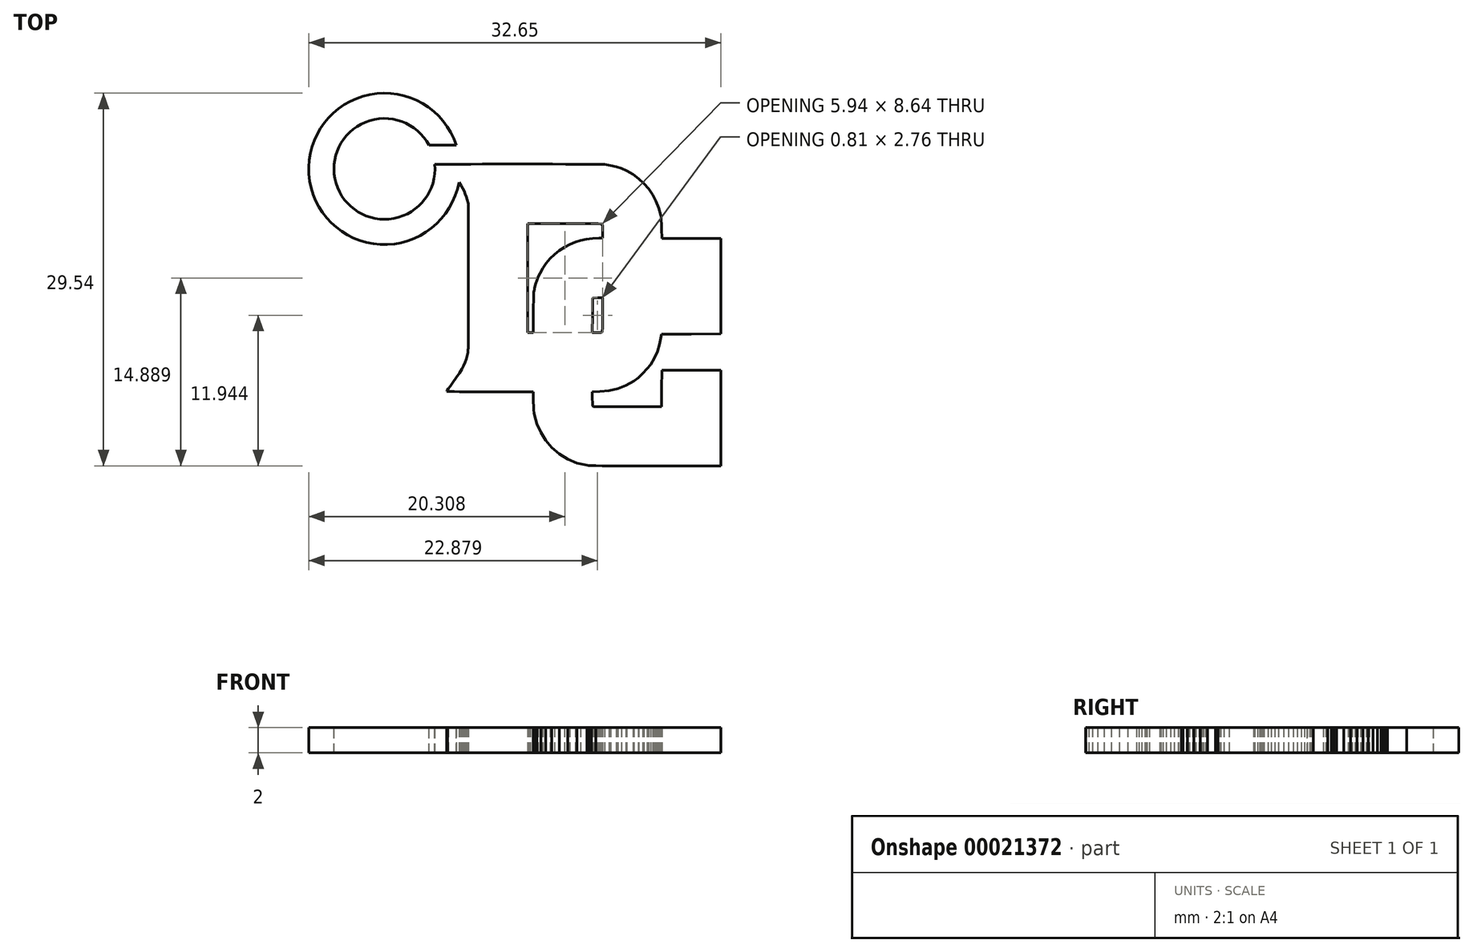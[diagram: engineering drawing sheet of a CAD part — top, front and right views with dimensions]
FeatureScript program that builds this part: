
annotation { "Feature Type Name" : "Feature", "Feature Type Description" : "" }
export const myFeature = defineFeature(function(context is Context, id is Id, definition is map)
    precondition{}
    {
        {
            var Q0;
            Q0=qCreatedBy(makeId("Top.planeOp"),FACE);
            var sketch = newSketch(context, id + "F0", { "sketchPlane" : qUnion([Q0])});
            skLineSegment(sketch, "E0", {"start": v(0.24, -11.91) * mm, "end": v(-0.53, -11.73) * mm});
            skLineSegment(sketch, "E1", {"start": v(-0.53, -11.73) * mm, "end": v(-1.26, -11.43) * mm});
            skLineSegment(sketch, "E2", {"start": v(-1.26, -11.43) * mm, "end": v(-1.93, -11.02) * mm});
            skLineSegment(sketch, "E3", {"start": v(-1.93, -11.02) * mm, "end": v(-2.53, -10.5) * mm});
            skLineSegment(sketch, "E4", {"start": v(-2.53, -10.5) * mm, "end": v(-3.02, -9.94) * mm});
            skLineSegment(sketch, "E5", {"start": v(-3.02, -9.94) * mm, "end": v(-3.41, -9.31) * mm});
            skLineSegment(sketch, "E6", {"start": v(-3.41, -9.31) * mm, "end": v(-3.72, -8.64) * mm});
            skLineSegment(sketch, "E7", {"start": v(-3.72, -8.64) * mm, "end": v(-3.92, -7.93) * mm});
            skLineSegment(sketch, "E8", {"start": v(-3.92, -7.93) * mm, "end": v(-3.95, -7.76) * mm});
            skLineSegment(sketch, "E9", {"start": v(-3.95, -7.76) * mm, "end": v(-3.97, -7.53) * mm});
            skLineSegment(sketch, "E10", {"start": v(-3.97, -7.53) * mm, "end": v(-3.98, -7.24) * mm});
            skLineSegment(sketch, "E11", {"start": v(-3.98, -7.24) * mm, "end": v(-4, -6.88) * mm});
            skLineSegment(sketch, "E12", {"start": v(-4, -6.88) * mm, "end": v(-4.01, -6.1) * mm});
            skLineSegment(sketch, "E13", {"start": v(-4.01, -6.1) * mm, "end": v(-7.44, -6.09) * mm});
            skLineSegment(sketch, "E14", {"start": v(-7.44, -6.09) * mm, "end": v(-8.12, -6.09) * mm});
            skLineSegment(sketch, "E15", {"start": v(-8.12, -6.09) * mm, "end": v(-8.77, -6.08) * mm});
            skLineSegment(sketch, "E16", {"start": v(-8.77, -6.08) * mm, "end": v(-9.35, -6.08) * mm});
            skLineSegment(sketch, "E17", {"start": v(-9.35, -6.08) * mm, "end": v(-9.85, -6.08) * mm});
            skLineSegment(sketch, "E18", {"start": v(-9.85, -6.08) * mm, "end": v(-10.27, -6.07) * mm});
            skLineSegment(sketch, "E19", {"start": v(-10.27, -6.07) * mm, "end": v(-10.59, -6.07) * mm});
            skLineSegment(sketch, "E20", {"start": v(-10.59, -6.07) * mm, "end": v(-10.79, -6.07) * mm});
            skLineSegment(sketch, "E21", {"start": v(-10.79, -6.07) * mm, "end": v(-10.86, -6.06) * mm});
            skLineSegment(sketch, "E22", {"start": v(-10.86, -6.06) * mm, "end": v(-10.82, -6) * mm});
            skLineSegment(sketch, "E23", {"start": v(-10.82, -6) * mm, "end": v(-10.72, -5.85) * mm});
            skLineSegment(sketch, "E24", {"start": v(-10.72, -5.85) * mm, "end": v(-10.57, -5.63) * mm});
            skLineSegment(sketch, "E25", {"start": v(-10.57, -5.63) * mm, "end": v(-10.38, -5.37) * mm});
            skLineSegment(sketch, "E26", {"start": v(-10.38, -5.37) * mm, "end": v(-10.09, -4.96) * mm});
            skLineSegment(sketch, "E27", {"start": v(-10.09, -4.96) * mm, "end": v(-9.85, -4.6) * mm});
            skLineSegment(sketch, "E28", {"start": v(-9.85, -4.6) * mm, "end": v(-9.66, -4.3) * mm});
            skLineSegment(sketch, "E29", {"start": v(-9.66, -4.3) * mm, "end": v(-9.51, -4.01) * mm});
            skLineSegment(sketch, "E30", {"start": v(-9.51, -4.01) * mm, "end": v(-9.4, -3.75) * mm});
            skLineSegment(sketch, "E31", {"start": v(-9.4, -3.75) * mm, "end": v(-9.3, -3.5) * mm});
            skLineSegment(sketch, "E32", {"start": v(-9.3, -3.5) * mm, "end": v(-9.24, -3.24) * mm});
            skLineSegment(sketch, "E33", {"start": v(-9.24, -3.24) * mm, "end": v(-9.18, -2.97) * mm});
            skLineSegment(sketch, "E34", {"start": v(-9.18, -2.97) * mm, "end": v(-9.18, -2.9) * mm});
            skLineSegment(sketch, "E35", {"start": v(-9.18, -2.9) * mm, "end": v(-9.17, -2.84) * mm});
            skLineSegment(sketch, "E36", {"start": v(-9.17, -2.84) * mm, "end": v(-9.16, -2.75) * mm});
            skLineSegment(sketch, "E37", {"start": v(-9.16, -2.75) * mm, "end": v(-9.16, -2.63) * mm});
            skLineSegment(sketch, "E38", {"start": v(-9.16, -2.63) * mm, "end": v(-9.15, -2.48) * mm});
            skLineSegment(sketch, "E39", {"start": v(-9.15, -2.48) * mm, "end": v(-9.15, -2.29) * mm});
            skLineSegment(sketch, "E40", {"start": v(-9.15, -2.29) * mm, "end": v(-9.15, -2.05) * mm});
            skLineSegment(sketch, "E41", {"start": v(-9.15, -2.05) * mm, "end": v(-9.14, -1.77) * mm});
            skLineSegment(sketch, "E42", {"start": v(-9.14, -1.77) * mm, "end": v(-9.14, -1.42) * mm});
            skLineSegment(sketch, "E43", {"start": v(-9.14, -1.42) * mm, "end": v(-9.14, -1.02) * mm});
            skLineSegment(sketch, "E44", {"start": v(-9.14, -1.02) * mm, "end": v(-9.14, -0.54) * mm});
            skLineSegment(sketch, "E45", {"start": v(-9.14, -0.54) * mm, "end": v(-9.14, 0) * mm});
            skLineSegment(sketch, "E46", {"start": v(-9.14, 0) * mm, "end": v(-9.14, 0.64) * mm});
            skLineSegment(sketch, "E47", {"start": v(-9.14, 0.64) * mm, "end": v(-9.14, 1.36) * mm});
            skLineSegment(sketch, "E48", {"start": v(-9.14, 1.36) * mm, "end": v(-9.14, 2.17) * mm});
            skLineSegment(sketch, "E49", {"start": v(-9.14, 2.17) * mm, "end": v(-9.14, 3.09) * mm});
            skLineSegment(sketch, "E50", {"start": v(-9.14, 3.09) * mm, "end": v(-9.15, 8.83) * mm});
            skLineSegment(sketch, "E51", {"start": v(-9.15, 8.83) * mm, "end": v(-9.24, 9.14) * mm});
            skLineSegment(sketch, "E52", {"start": v(-9.24, 9.14) * mm, "end": v(-9.3, 9.38) * mm});
            skLineSegment(sketch, "E53", {"start": v(-9.3, 9.38) * mm, "end": v(-9.39, 9.6) * mm});
            skLineSegment(sketch, "E54", {"start": v(-9.39, 9.6) * mm, "end": v(-9.48, 9.81) * mm});
            skLineSegment(sketch, "E55", {"start": v(-9.48, 9.81) * mm, "end": v(-9.59, 10.03) * mm});
            skLineSegment(sketch, "E56", {"start": v(-9.59, 10.03) * mm, "end": v(-9.72, 10.26) * mm});
            skLineSegment(sketch, "E57", {"start": v(-9.72, 10.26) * mm, "end": v(-9.89, 10.52) * mm});
            skLineSegment(sketch, "E58", {"start": v(-9.89, 10.52) * mm, "end": v(-10.1, 10.83) * mm});
            skLineSegment(sketch, "E59", {"start": v(-10.1, 10.83) * mm, "end": v(-10.34, 11.18) * mm});
            skLineSegment(sketch, "E60", {"start": v(-10.34, 11.18) * mm, "end": v(-10.54, 11.47) * mm});
            skLineSegment(sketch, "E61", {"start": v(-10.54, 11.47) * mm, "end": v(-10.7, 11.7) * mm});
            skLineSegment(sketch, "E62", {"start": v(-10.7, 11.7) * mm, "end": v(-10.82, 11.87) * mm});
            skLineSegment(sketch, "E63", {"start": v(-10.82, 11.87) * mm, "end": v(-10.86, 11.94) * mm});
            skLineSegment(sketch, "E64", {"start": v(-10.86, 11.94) * mm, "end": v(-10.72, 11.94) * mm});
            skLineSegment(sketch, "E65", {"start": v(-10.72, 11.94) * mm, "end": v(-10.34, 11.95) * mm});
            skLineSegment(sketch, "E66", {"start": v(-10.34, 11.95) * mm, "end": v(-9.74, 11.95) * mm});
            skLineSegment(sketch, "E67", {"start": v(-9.74, 11.95) * mm, "end": v(-8.96, 11.96) * mm});
            skLineSegment(sketch, "E68", {"start": v(-8.96, 11.96) * mm, "end": v(-8.03, 11.96) * mm});
            skLineSegment(sketch, "E69", {"start": v(-8.03, 11.96) * mm, "end": v(-7, 11.96) * mm});
            skLineSegment(sketch, "E70", {"start": v(-7, 11.96) * mm, "end": v(-5.9, 11.96) * mm});
            skLineSegment(sketch, "E71", {"start": v(-5.9, 11.96) * mm, "end": v(-4.75, 11.96) * mm});
            skLineSegment(sketch, "E72", {"start": v(-4.75, 11.96) * mm, "end": v(-3.6, 11.96) * mm});
            skLineSegment(sketch, "E73", {"start": v(-3.6, 11.96) * mm, "end": v(-2.47, 11.96) * mm});
            skLineSegment(sketch, "E74", {"start": v(-2.47, 11.96) * mm, "end": v(-1.42, 11.96) * mm});
            skLineSegment(sketch, "E75", {"start": v(-1.42, 11.96) * mm, "end": v(-0.46, 11.95) * mm});
            skLineSegment(sketch, "E76", {"start": v(-0.46, 11.95) * mm, "end": v(0.36, 11.95) * mm});
            skLineSegment(sketch, "E77", {"start": v(0.36, 11.95) * mm, "end": v(1, 11.94) * mm});
            skLineSegment(sketch, "E78", {"start": v(1, 11.94) * mm, "end": v(1.45, 11.94) * mm});
            skLineSegment(sketch, "E79", {"start": v(1.45, 11.94) * mm, "end": v(1.65, 11.93) * mm});
            skLineSegment(sketch, "E80", {"start": v(1.65, 11.93) * mm, "end": v(2.12, 11.86) * mm});
            skLineSegment(sketch, "E81", {"start": v(2.12, 11.86) * mm, "end": v(2.56, 11.76) * mm});
            skLineSegment(sketch, "E82", {"start": v(2.56, 11.76) * mm, "end": v(2.97, 11.61) * mm});
            skLineSegment(sketch, "E83", {"start": v(2.97, 11.61) * mm, "end": v(3.4, 11.42) * mm});
            skLineSegment(sketch, "E84", {"start": v(3.4, 11.42) * mm, "end": v(3.9, 11.14) * mm});
            skLineSegment(sketch, "E85", {"start": v(3.9, 11.14) * mm, "end": v(4.35, 10.8) * mm});
            skLineSegment(sketch, "E86", {"start": v(4.35, 10.8) * mm, "end": v(4.76, 10.42) * mm});
            skLineSegment(sketch, "E87", {"start": v(4.76, 10.42) * mm, "end": v(5.13, 10) * mm});
            skLineSegment(sketch, "E88", {"start": v(5.13, 10) * mm, "end": v(5.45, 9.53) * mm});
            skLineSegment(sketch, "E89", {"start": v(5.45, 9.53) * mm, "end": v(5.71, 9.02) * mm});
            skLineSegment(sketch, "E90", {"start": v(5.71, 9.02) * mm, "end": v(5.93, 8.48) * mm});
            skLineSegment(sketch, "E91", {"start": v(5.93, 8.48) * mm, "end": v(6.08, 7.92) * mm});
            skLineSegment(sketch, "E92", {"start": v(6.08, 7.92) * mm, "end": v(6.12, 7.72) * mm});
            skLineSegment(sketch, "E93", {"start": v(6.12, 7.72) * mm, "end": v(6.14, 7.5) * mm});
            skLineSegment(sketch, "E94", {"start": v(6.14, 7.5) * mm, "end": v(6.16, 7.22) * mm});
            skLineSegment(sketch, "E95", {"start": v(6.16, 7.22) * mm, "end": v(6.17, 6.83) * mm});
            skLineSegment(sketch, "E96", {"start": v(6.17, 6.83) * mm, "end": v(6.19, 6.08) * mm});
            skLineSegment(sketch, "E97", {"start": v(6.19, 6.08) * mm, "end": v(10.86, 6.08) * mm});
            skLineSegment(sketch, "E98", {"start": v(10.86, 6.08) * mm, "end": v(10.86, -1.5) * mm});
            skLineSegment(sketch, "E99", {"start": v(10.86, -1.5) * mm, "end": v(8.51, -1.5) * mm});
            skLineSegment(sketch, "E100", {"start": v(8.51, -1.5) * mm, "end": v(6.16, -1.51) * mm});
            skLineSegment(sketch, "E101", {"start": v(6.16, -1.51) * mm, "end": v(6.14, -1.67) * mm});
            skLineSegment(sketch, "E102", {"start": v(6.14, -1.67) * mm, "end": v(6, -2.31) * mm});
            skLineSegment(sketch, "E103", {"start": v(6, -2.31) * mm, "end": v(5.83, -2.88) * mm});
            skLineSegment(sketch, "E104", {"start": v(5.83, -2.88) * mm, "end": v(5.6, -3.41) * mm});
            skLineSegment(sketch, "E105", {"start": v(5.6, -3.41) * mm, "end": v(5.29, -3.92) * mm});
            skLineSegment(sketch, "E106", {"start": v(5.29, -3.92) * mm, "end": v(5.02, -4.25) * mm});
            skLineSegment(sketch, "E107", {"start": v(5.02, -4.25) * mm, "end": v(4.68, -4.62) * mm});
            skLineSegment(sketch, "E108", {"start": v(4.68, -4.62) * mm, "end": v(4.3, -4.97) * mm});
            skLineSegment(sketch, "E109", {"start": v(4.3, -4.97) * mm, "end": v(3.97, -5.23) * mm});
            skLineSegment(sketch, "E110", {"start": v(3.97, -5.23) * mm, "end": v(3.34, -5.6) * mm});
            skLineSegment(sketch, "E111", {"start": v(3.34, -5.6) * mm, "end": v(2.7, -5.85) * mm});
            skLineSegment(sketch, "E112", {"start": v(2.7, -5.85) * mm, "end": v(2.01, -6) * mm});
            skLineSegment(sketch, "E113", {"start": v(2.01, -6) * mm, "end": v(1.26, -6.07) * mm});
            skLineSegment(sketch, "E114", {"start": v(1.26, -6.07) * mm, "end": v(0.68, -6.09) * mm});
            skLineSegment(sketch, "E115", {"start": v(0.68, -6.09) * mm, "end": v(0.68, -6.65) * mm});
            skLineSegment(sketch, "E116", {"start": v(0.68, -6.65) * mm, "end": v(0.68, -6.92) * mm});
            skLineSegment(sketch, "E117", {"start": v(0.68, -6.92) * mm, "end": v(0.7, -7.1) * mm});
            skLineSegment(sketch, "E118", {"start": v(0.7, -7.1) * mm, "end": v(0.7, -7.2) * mm});
            skLineSegment(sketch, "E119", {"start": v(0.7, -7.2) * mm, "end": v(0.73, -7.25) * mm});
            skLineSegment(sketch, "E120", {"start": v(0.73, -7.25) * mm, "end": v(0.77, -7.26) * mm});
            skLineSegment(sketch, "E121", {"start": v(0.77, -7.26) * mm, "end": v(0.9, -7.26) * mm});
            skLineSegment(sketch, "E122", {"start": v(0.9, -7.26) * mm, "end": v(1.09, -7.27) * mm});
            skLineSegment(sketch, "E123", {"start": v(1.09, -7.27) * mm, "end": v(1.37, -7.27) * mm});
            skLineSegment(sketch, "E124", {"start": v(1.37, -7.27) * mm, "end": v(1.74, -7.28) * mm});
            skLineSegment(sketch, "E125", {"start": v(1.74, -7.28) * mm, "end": v(2.21, -7.28) * mm});
            skLineSegment(sketch, "E126", {"start": v(2.21, -7.28) * mm, "end": v(2.79, -7.28) * mm});
            skLineSegment(sketch, "E127", {"start": v(2.79, -7.28) * mm, "end": v(3.47, -7.27) * mm});
            skLineSegment(sketch, "E128", {"start": v(3.47, -7.27) * mm, "end": v(6.16, -7.27) * mm});
            skLineSegment(sketch, "E129", {"start": v(6.16, -7.27) * mm, "end": v(6.17, -5.83) * mm});
            skLineSegment(sketch, "E130", {"start": v(6.17, -5.83) * mm, "end": v(6.18, -4.39) * mm});
            skLineSegment(sketch, "E131", {"start": v(6.18, -4.39) * mm, "end": v(10.86, -4.39) * mm});
            skLineSegment(sketch, "E132", {"start": v(10.86, -4.39) * mm, "end": v(10.86, -11.96) * mm});
            skLineSegment(sketch, "E133", {"start": v(10.86, -11.96) * mm, "end": v(5.7, -11.96) * mm});
            skLineSegment(sketch, "E134", {"start": v(5.7, -11.96) * mm, "end": v(4.26, -11.96) * mm});
            skLineSegment(sketch, "E135", {"start": v(4.26, -11.96) * mm, "end": v(3.1, -11.96) * mm});
            skLineSegment(sketch, "E136", {"start": v(3.1, -11.96) * mm, "end": v(2.18, -11.95) * mm});
            skLineSegment(sketch, "E137", {"start": v(2.18, -11.95) * mm, "end": v(1.47, -11.95) * mm});
            skLineSegment(sketch, "E138", {"start": v(1.47, -11.95) * mm, "end": v(0.96, -11.94) * mm});
            skLineSegment(sketch, "E139", {"start": v(0.96, -11.94) * mm, "end": v(0.6, -11.94) * mm});
            skLineSegment(sketch, "E140", {"start": v(0.6, -11.94) * mm, "end": v(0.37, -11.93) * mm});
            skLineSegment(sketch, "E141", {"start": v(0.37, -11.93) * mm, "end": v(0.24, -11.91) * mm});
            skLineSegment(sketch, "E142", {"start": v(-4, 0.21) * mm, "end": v(-3.99, 0.73) * mm});
            skLineSegment(sketch, "E143", {"start": v(-3.99, 0.73) * mm, "end": v(-3.98, 1.13) * mm});
            skLineSegment(sketch, "E144", {"start": v(-3.98, 1.13) * mm, "end": v(-3.98, 1.42) * mm});
            skLineSegment(sketch, "E145", {"start": v(-3.98, 1.42) * mm, "end": v(-3.97, 1.64) * mm});
            skLineSegment(sketch, "E146", {"start": v(-3.97, 1.64) * mm, "end": v(-3.96, 1.8) * mm});
            skLineSegment(sketch, "E147", {"start": v(-3.96, 1.8) * mm, "end": v(-3.94, 1.92) * mm});
            skLineSegment(sketch, "E148", {"start": v(-3.94, 1.92) * mm, "end": v(-3.92, 2.03) * mm});
            skLineSegment(sketch, "E149", {"start": v(-3.92, 2.03) * mm, "end": v(-3.9, 2.15) * mm});
            skLineSegment(sketch, "E150", {"start": v(-3.9, 2.15) * mm, "end": v(-3.8, 2.47) * mm});
            skLineSegment(sketch, "E151", {"start": v(-3.8, 2.47) * mm, "end": v(-3.72, 2.75) * mm});
            skLineSegment(sketch, "E152", {"start": v(-3.72, 2.75) * mm, "end": v(-3.62, 3) * mm});
            skLineSegment(sketch, "E153", {"start": v(-3.62, 3) * mm, "end": v(-3.48, 3.3) * mm});
            skLineSegment(sketch, "E154", {"start": v(-3.48, 3.3) * mm, "end": v(-3.24, 3.71) * mm});
            skLineSegment(sketch, "E155", {"start": v(-3.24, 3.71) * mm, "end": v(-2.97, 4.1) * mm});
            skLineSegment(sketch, "E156", {"start": v(-2.97, 4.1) * mm, "end": v(-2.66, 4.47) * mm});
            skLineSegment(sketch, "E157", {"start": v(-2.66, 4.47) * mm, "end": v(-2.31, 4.8) * mm});
            skLineSegment(sketch, "E158", {"start": v(-2.31, 4.8) * mm, "end": v(-1.94, 5.1) * mm});
            skLineSegment(sketch, "E159", {"start": v(-1.94, 5.1) * mm, "end": v(-1.54, 5.37) * mm});
            skLineSegment(sketch, "E160", {"start": v(-1.54, 5.37) * mm, "end": v(-1.12, 5.6) * mm});
            skLineSegment(sketch, "E161", {"start": v(-1.12, 5.6) * mm, "end": v(-0.68, 5.78) * mm});
            skLineSegment(sketch, "E162", {"start": v(-0.68, 5.78) * mm, "end": v(-0.27, 5.9) * mm});
            skLineSegment(sketch, "E163", {"start": v(-0.27, 5.9) * mm, "end": v(0.19, 6) * mm});
            skLineSegment(sketch, "E164", {"start": v(0.19, 6) * mm, "end": v(0.68, 6.06) * mm});
            skLineSegment(sketch, "E165", {"start": v(0.68, 6.06) * mm, "end": v(1.22, 6.09) * mm});
            skLineSegment(sketch, "E166", {"start": v(1.22, 6.09) * mm, "end": v(1.48, 6.1) * mm});
            skLineSegment(sketch, "E167", {"start": v(1.48, 6.1) * mm, "end": v(1.49, 6.63) * mm});
            skLineSegment(sketch, "E168", {"start": v(1.49, 6.63) * mm, "end": v(1.49, 6.87) * mm});
            skLineSegment(sketch, "E169", {"start": v(1.49, 6.87) * mm, "end": v(1.49, 7.04) * mm});
            skLineSegment(sketch, "E170", {"start": v(1.49, 7.04) * mm, "end": v(1.48, 7.15) * mm});
            skLineSegment(sketch, "E171", {"start": v(1.48, 7.15) * mm, "end": v(1.46, 7.2) * mm});
            skLineSegment(sketch, "E172", {"start": v(1.46, 7.2) * mm, "end": v(1.42, 7.22) * mm});
            skLineSegment(sketch, "E173", {"start": v(1.42, 7.22) * mm, "end": v(1.33, 7.23) * mm});
            skLineSegment(sketch, "E174", {"start": v(1.33, 7.23) * mm, "end": v(1.15, 7.23) * mm});
            skLineSegment(sketch, "E175", {"start": v(1.15, 7.23) * mm, "end": v(0.88, 7.24) * mm});
            skLineSegment(sketch, "E176", {"start": v(0.88, 7.24) * mm, "end": v(0.5, 7.24) * mm});
            skLineSegment(sketch, "E177", {"start": v(0.5, 7.24) * mm, "end": v(-0.02, 7.25) * mm});
            skLineSegment(sketch, "E178", {"start": v(-0.02, 7.25) * mm, "end": v(-0.68, 7.25) * mm});
            skLineSegment(sketch, "E179", {"start": v(-0.68, 7.25) * mm, "end": v(-1.52, 7.25) * mm});
            skLineSegment(sketch, "E180", {"start": v(-1.52, 7.25) * mm, "end": v(-4.45, 7.25) * mm});
            skLineSegment(sketch, "E181", {"start": v(-4.45, 7.25) * mm, "end": v(-4.45, 2.95) * mm});
            skLineSegment(sketch, "E182", {"start": v(-4.45, 2.95) * mm, "end": v(-4.45, 2.08) * mm});
            skLineSegment(sketch, "E183", {"start": v(-4.45, 2.08) * mm, "end": v(-4.45, 1.27) * mm});
            skLineSegment(sketch, "E184", {"start": v(-4.45, 1.27) * mm, "end": v(-4.45, 0.54) * mm});
            skLineSegment(sketch, "E185", {"start": v(-4.45, 0.54) * mm, "end": v(-4.45, -0.1) * mm});
            skLineSegment(sketch, "E186", {"start": v(-4.45, -0.1) * mm, "end": v(-4.44, -0.63) * mm});
            skLineSegment(sketch, "E187", {"start": v(-4.44, -0.63) * mm, "end": v(-4.44, -1.03) * mm});
            skLineSegment(sketch, "E188", {"start": v(-4.44, -1.03) * mm, "end": v(-4.44, -1.29) * mm});
            skLineSegment(sketch, "E189", {"start": v(-4.44, -1.29) * mm, "end": v(-4.43, -1.38) * mm});
            skLineSegment(sketch, "E190", {"start": v(-4.43, -1.38) * mm, "end": v(-4.36, -1.4) * mm});
            skLineSegment(sketch, "E191", {"start": v(-4.36, -1.4) * mm, "end": v(-4.21, -1.4) * mm});
            skLineSegment(sketch, "E192", {"start": v(-4.21, -1.4) * mm, "end": v(-4.01, -1.38) * mm});
            skLineSegment(sketch, "E193", {"start": v(-4.01, -1.38) * mm, "end": v(-4, 0.21) * mm});
            skLineSegment(sketch, "E194", {"start": v(1.46, -1.36) * mm, "end": v(1.47, -1.27) * mm});
            skLineSegment(sketch, "E195", {"start": v(1.47, -1.27) * mm, "end": v(1.49, -1.03) * mm});
            skLineSegment(sketch, "E196", {"start": v(1.49, -1.03) * mm, "end": v(1.5, -0.61) * mm});
            skLineSegment(sketch, "E197", {"start": v(1.5, -0.61) * mm, "end": v(1.5, 0.02) * mm});
            skLineSegment(sketch, "E198", {"start": v(1.5, 0.02) * mm, "end": v(1.5, 1.37) * mm});
            skLineSegment(sketch, "E199", {"start": v(1.5, 1.37) * mm, "end": v(1.1, 1.36) * mm});
            skLineSegment(sketch, "E200", {"start": v(1.1, 1.36) * mm, "end": v(0.7, 1.35) * mm});
            skLineSegment(sketch, "E201", {"start": v(0.7, 1.35) * mm, "end": v(0.7, -0.02) * mm});
            skLineSegment(sketch, "E202", {"start": v(0.7, -0.02) * mm, "end": v(0.68, -1.4) * mm});
            skLineSegment(sketch, "E203", {"start": v(0.68, -1.4) * mm, "end": v(1.05, -1.4) * mm});
            skLineSegment(sketch, "E204", {"start": v(1.05, -1.4) * mm, "end": v(1.21, -1.4) * mm});
            skLineSegment(sketch, "E205", {"start": v(1.21, -1.4) * mm, "end": v(1.33, -1.39) * mm});
            skLineSegment(sketch, "E206", {"start": v(1.33, -1.39) * mm, "end": v(1.42, -1.38) * mm});
            skLineSegment(sketch, "E207", {"start": v(1.42, -1.38) * mm, "end": v(1.46, -1.36) * mm});
            skSolve(sketch);
        }
        {
            var Q0;
            Q0 = qSketchRegion(id + "F0", true);
            extrude(context, id + "F1", {"entities" : qUnion([Q0]), "depth" : 2 * mm});
        }
        {
            var Q0;
            Q0=makeQuery(id+"F1.opExtrude","CAP_FACE",FACE,{"disambiguationData":[OSD([sQuery(id+"F0.wireOp",EDGE,"E0"),sQuery(id+"F0.wireOp",EDGE,"E1"),sQuery(id+"F0.wireOp",EDGE,"E2"),sQuery(id+"F0.wireOp",EDGE,"E3"),sQuery(id+"F0.wireOp",EDGE,"E4"),sQuery(id+"F0.wireOp",EDGE,"E5"),sQuery(id+"F0.wireOp",EDGE,"E6"),sQuery(id+"F0.wireOp",EDGE,"E7"),sQuery(id+"F0.wireOp",EDGE,"E8"),sQuery(id+"F0.wireOp",EDGE,"E9"),sQuery(id+"F0.wireOp",EDGE,"E10"),sQuery(id+"F0.wireOp",EDGE,"E11"),sQuery(id+"F0.wireOp",EDGE,"E12"),sQuery(id+"F0.wireOp",EDGE,"E13"),sQuery(id+"F0.wireOp",EDGE,"E14"),sQuery(id+"F0.wireOp",EDGE,"E15"),sQuery(id+"F0.wireOp",EDGE,"E16"),sQuery(id+"F0.wireOp",EDGE,"E17"),sQuery(id+"F0.wireOp",EDGE,"E18"),sQuery(id+"F0.wireOp",EDGE,"E19"),sQuery(id+"F0.wireOp",EDGE,"E20"),sQuery(id+"F0.wireOp",EDGE,"E21"),sQuery(id+"F0.wireOp",EDGE,"E22"),sQuery(id+"F0.wireOp",EDGE,"E23"),sQuery(id+"F0.wireOp",EDGE,"E24"),sQuery(id+"F0.wireOp",EDGE,"E25"),sQuery(id+"F0.wireOp",EDGE,"E26"),sQuery(id+"F0.wireOp",EDGE,"E27"),sQuery(id+"F0.wireOp",EDGE,"E28"),sQuery(id+"F0.wireOp",EDGE,"E29"),sQuery(id+"F0.wireOp",EDGE,"E30"),sQuery(id+"F0.wireOp",EDGE,"E31"),sQuery(id+"F0.wireOp",EDGE,"E32"),sQuery(id+"F0.wireOp",EDGE,"E33"),sQuery(id+"F0.wireOp",EDGE,"E34"),sQuery(id+"F0.wireOp",EDGE,"E35"),sQuery(id+"F0.wireOp",EDGE,"E36"),sQuery(id+"F0.wireOp",EDGE,"E37"),sQuery(id+"F0.wireOp",EDGE,"E38"),sQuery(id+"F0.wireOp",EDGE,"E39"),sQuery(id+"F0.wireOp",EDGE,"E40"),sQuery(id+"F0.wireOp",EDGE,"E41"),sQuery(id+"F0.wireOp",EDGE,"E42"),sQuery(id+"F0.wireOp",EDGE,"E43"),sQuery(id+"F0.wireOp",EDGE,"E44"),sQuery(id+"F0.wireOp",EDGE,"E45"),sQuery(id+"F0.wireOp",EDGE,"E46"),sQuery(id+"F0.wireOp",EDGE,"E47"),sQuery(id+"F0.wireOp",EDGE,"E48"),sQuery(id+"F0.wireOp",EDGE,"E49"),sQuery(id+"F0.wireOp",EDGE,"E50"),sQuery(id+"F0.wireOp",EDGE,"E51"),sQuery(id+"F0.wireOp",EDGE,"E52"),sQuery(id+"F0.wireOp",EDGE,"E53"),sQuery(id+"F0.wireOp",EDGE,"E54"),sQuery(id+"F0.wireOp",EDGE,"E55"),sQuery(id+"F0.wireOp",EDGE,"E56"),sQuery(id+"F0.wireOp",EDGE,"E57"),sQuery(id+"F0.wireOp",EDGE,"E58"),sQuery(id+"F0.wireOp",EDGE,"E59"),sQuery(id+"F0.wireOp",EDGE,"E60"),sQuery(id+"F0.wireOp",EDGE,"E61"),sQuery(id+"F0.wireOp",EDGE,"E62"),sQuery(id+"F0.wireOp",EDGE,"E63"),sQuery(id+"F0.wireOp",EDGE,"E64"),sQuery(id+"F0.wireOp",EDGE,"E65"),sQuery(id+"F0.wireOp",EDGE,"E66"),sQuery(id+"F0.wireOp",EDGE,"E67"),sQuery(id+"F0.wireOp",EDGE,"E68"),sQuery(id+"F0.wireOp",EDGE,"E69"),sQuery(id+"F0.wireOp",EDGE,"E70"),sQuery(id+"F0.wireOp",EDGE,"E71"),sQuery(id+"F0.wireOp",EDGE,"E72"),sQuery(id+"F0.wireOp",EDGE,"E73"),sQuery(id+"F0.wireOp",EDGE,"E74"),sQuery(id+"F0.wireOp",EDGE,"E75"),sQuery(id+"F0.wireOp",EDGE,"E76"),sQuery(id+"F0.wireOp",EDGE,"E77"),sQuery(id+"F0.wireOp",EDGE,"E78"),sQuery(id+"F0.wireOp",EDGE,"E79"),sQuery(id+"F0.wireOp",EDGE,"E80"),sQuery(id+"F0.wireOp",EDGE,"E81"),sQuery(id+"F0.wireOp",EDGE,"E82"),sQuery(id+"F0.wireOp",EDGE,"E83"),sQuery(id+"F0.wireOp",EDGE,"E84"),sQuery(id+"F0.wireOp",EDGE,"E85"),sQuery(id+"F0.wireOp",EDGE,"E86"),sQuery(id+"F0.wireOp",EDGE,"E87"),sQuery(id+"F0.wireOp",EDGE,"E88"),sQuery(id+"F0.wireOp",EDGE,"E89"),sQuery(id+"F0.wireOp",EDGE,"E90"),sQuery(id+"F0.wireOp",EDGE,"E91"),sQuery(id+"F0.wireOp",EDGE,"E92"),sQuery(id+"F0.wireOp",EDGE,"E93"),sQuery(id+"F0.wireOp",EDGE,"E94"),sQuery(id+"F0.wireOp",EDGE,"E95"),sQuery(id+"F0.wireOp",EDGE,"E96"),sQuery(id+"F0.wireOp",EDGE,"E97"),sQuery(id+"F0.wireOp",EDGE,"E98"),sQuery(id+"F0.wireOp",EDGE,"E99"),sQuery(id+"F0.wireOp",EDGE,"E100"),sQuery(id+"F0.wireOp",EDGE,"E101"),sQuery(id+"F0.wireOp",EDGE,"E102"),sQuery(id+"F0.wireOp",EDGE,"E103"),sQuery(id+"F0.wireOp",EDGE,"E104"),sQuery(id+"F0.wireOp",EDGE,"E105"),sQuery(id+"F0.wireOp",EDGE,"E106"),sQuery(id+"F0.wireOp",EDGE,"E107"),sQuery(id+"F0.wireOp",EDGE,"E108"),sQuery(id+"F0.wireOp",EDGE,"E109"),sQuery(id+"F0.wireOp",EDGE,"E110"),sQuery(id+"F0.wireOp",EDGE,"E111"),sQuery(id+"F0.wireOp",EDGE,"E112"),sQuery(id+"F0.wireOp",EDGE,"E113"),sQuery(id+"F0.wireOp",EDGE,"E114"),sQuery(id+"F0.wireOp",EDGE,"E115"),sQuery(id+"F0.wireOp",EDGE,"E116"),sQuery(id+"F0.wireOp",EDGE,"E117"),sQuery(id+"F0.wireOp",EDGE,"E118"),sQuery(id+"F0.wireOp",EDGE,"E119"),sQuery(id+"F0.wireOp",EDGE,"E120"),sQuery(id+"F0.wireOp",EDGE,"E121"),sQuery(id+"F0.wireOp",EDGE,"E122"),sQuery(id+"F0.wireOp",EDGE,"E123"),sQuery(id+"F0.wireOp",EDGE,"E124"),sQuery(id+"F0.wireOp",EDGE,"E125"),sQuery(id+"F0.wireOp",EDGE,"E126"),sQuery(id+"F0.wireOp",EDGE,"E127"),sQuery(id+"F0.wireOp",EDGE,"E128"),sQuery(id+"F0.wireOp",EDGE,"E129"),sQuery(id+"F0.wireOp",EDGE,"E130"),sQuery(id+"F0.wireOp",EDGE,"E131"),sQuery(id+"F0.wireOp",EDGE,"E132"),sQuery(id+"F0.wireOp",EDGE,"E133"),sQuery(id+"F0.wireOp",EDGE,"E134"),sQuery(id+"F0.wireOp",EDGE,"E135"),sQuery(id+"F0.wireOp",EDGE,"E136"),sQuery(id+"F0.wireOp",EDGE,"E137"),sQuery(id+"F0.wireOp",EDGE,"E138"),sQuery(id+"F0.wireOp",EDGE,"E139"),sQuery(id+"F0.wireOp",EDGE,"E140"),sQuery(id+"F0.wireOp",EDGE,"E141"),sQuery(id+"F0.wireOp",EDGE,"E142"),sQuery(id+"F0.wireOp",EDGE,"E143"),sQuery(id+"F0.wireOp",EDGE,"E144"),sQuery(id+"F0.wireOp",EDGE,"E145"),sQuery(id+"F0.wireOp",EDGE,"E146"),sQuery(id+"F0.wireOp",EDGE,"E147"),sQuery(id+"F0.wireOp",EDGE,"E148"),sQuery(id+"F0.wireOp",EDGE,"E149"),sQuery(id+"F0.wireOp",EDGE,"E150"),sQuery(id+"F0.wireOp",EDGE,"E151"),sQuery(id+"F0.wireOp",EDGE,"E152"),sQuery(id+"F0.wireOp",EDGE,"E153"),sQuery(id+"F0.wireOp",EDGE,"E154"),sQuery(id+"F0.wireOp",EDGE,"E155"),sQuery(id+"F0.wireOp",EDGE,"E156"),sQuery(id+"F0.wireOp",EDGE,"E157"),sQuery(id+"F0.wireOp",EDGE,"E158"),sQuery(id+"F0.wireOp",EDGE,"E159"),sQuery(id+"F0.wireOp",EDGE,"E160"),sQuery(id+"F0.wireOp",EDGE,"E161"),sQuery(id+"F0.wireOp",EDGE,"E162"),sQuery(id+"F0.wireOp",EDGE,"E163"),sQuery(id+"F0.wireOp",EDGE,"E164"),sQuery(id+"F0.wireOp",EDGE,"E165"),sQuery(id+"F0.wireOp",EDGE,"E166"),sQuery(id+"F0.wireOp",EDGE,"E167"),sQuery(id+"F0.wireOp",EDGE,"E168"),sQuery(id+"F0.wireOp",EDGE,"E169"),sQuery(id+"F0.wireOp",EDGE,"E170"),sQuery(id+"F0.wireOp",EDGE,"E171"),sQuery(id+"F0.wireOp",EDGE,"E172"),sQuery(id+"F0.wireOp",EDGE,"E173"),sQuery(id+"F0.wireOp",EDGE,"E174"),sQuery(id+"F0.wireOp",EDGE,"E175"),sQuery(id+"F0.wireOp",EDGE,"E176"),sQuery(id+"F0.wireOp",EDGE,"E177"),sQuery(id+"F0.wireOp",EDGE,"E178"),sQuery(id+"F0.wireOp",EDGE,"E179"),sQuery(id+"F0.wireOp",EDGE,"E180"),sQuery(id+"F0.wireOp",EDGE,"E181"),sQuery(id+"F0.wireOp",EDGE,"E182"),sQuery(id+"F0.wireOp",EDGE,"E183"),sQuery(id+"F0.wireOp",EDGE,"E184"),sQuery(id+"F0.wireOp",EDGE,"E185"),sQuery(id+"F0.wireOp",EDGE,"E186"),sQuery(id+"F0.wireOp",EDGE,"E187"),sQuery(id+"F0.wireOp",EDGE,"E188"),sQuery(id+"F0.wireOp",EDGE,"E189"),sQuery(id+"F0.wireOp",EDGE,"E190"),sQuery(id+"F0.wireOp",EDGE,"E191"),sQuery(id+"F0.wireOp",EDGE,"E192"),sQuery(id+"F0.wireOp",EDGE,"E193"),sQuery(id+"F0.wireOp",EDGE,"E194"),sQuery(id+"F0.wireOp",EDGE,"E195"),sQuery(id+"F0.wireOp",EDGE,"E196"),sQuery(id+"F0.wireOp",EDGE,"E197"),sQuery(id+"F0.wireOp",EDGE,"E198"),sQuery(id+"F0.wireOp",EDGE,"E199"),sQuery(id+"F0.wireOp",EDGE,"E200"),sQuery(id+"F0.wireOp",EDGE,"E201"),sQuery(id+"F0.wireOp",EDGE,"E202"),sQuery(id+"F0.wireOp",EDGE,"E203"),sQuery(id+"F0.wireOp",EDGE,"E204"),sQuery(id+"F0.wireOp",EDGE,"E205"),sQuery(id+"F0.wireOp",EDGE,"E206"),sQuery(id+"F0.wireOp",EDGE,"E207")])],"isStart":false});
            var sketch = newSketch(context, id + "F2", { "sketchPlane" : qUnion([Q0])});
            skArc(sketch, "E208", {"start": v(-10.1, 13.45) * mm, "mid": v(-21.78, 11.17) * mm, "end": v(-9.89, 10.52) * mm});
            skArc(sketch, "E209", {"start": v(-12.26, 13.45) * mm, "mid": v(-19.63, 10.45) * mm, "end": v(-11.8, 11.94) * mm});
            skLineSegment(sketch, "E210", {"start": v(-12.26, 13.45) * mm, "end": v(-10.1, 13.45) * mm});
            skLineSegment(sketch, "E211", {"start": v(-11.8, 11.94) * mm, "end": v(-10.86, 11.94) * mm});
            skSolve(sketch);
        }
        {
            var Q0;
            Q0=makeQuery(id+"F2.imprint","IMPRINT",FACE,{"disambiguationData":[TD([[makeQuery(id+"F2.imprint","IMPRINT",EDGE,{"derivedFrom":sQuery(id+"F2.wireOp",EDGE,"E208")}),1.0]])]});
            var Q1;
            Q1=makeQuery(id+"F1.opExtrude","CAP_FACE",FACE,{"disambiguationData":[OSD([sQuery(id+"F0.wireOp",EDGE,"E0"),sQuery(id+"F0.wireOp",EDGE,"E1"),sQuery(id+"F0.wireOp",EDGE,"E2"),sQuery(id+"F0.wireOp",EDGE,"E3"),sQuery(id+"F0.wireOp",EDGE,"E4"),sQuery(id+"F0.wireOp",EDGE,"E5"),sQuery(id+"F0.wireOp",EDGE,"E6"),sQuery(id+"F0.wireOp",EDGE,"E7"),sQuery(id+"F0.wireOp",EDGE,"E8"),sQuery(id+"F0.wireOp",EDGE,"E9"),sQuery(id+"F0.wireOp",EDGE,"E10"),sQuery(id+"F0.wireOp",EDGE,"E11"),sQuery(id+"F0.wireOp",EDGE,"E12"),sQuery(id+"F0.wireOp",EDGE,"E13"),sQuery(id+"F0.wireOp",EDGE,"E14"),sQuery(id+"F0.wireOp",EDGE,"E15"),sQuery(id+"F0.wireOp",EDGE,"E16"),sQuery(id+"F0.wireOp",EDGE,"E17"),sQuery(id+"F0.wireOp",EDGE,"E18"),sQuery(id+"F0.wireOp",EDGE,"E19"),sQuery(id+"F0.wireOp",EDGE,"E20"),sQuery(id+"F0.wireOp",EDGE,"E21"),sQuery(id+"F0.wireOp",EDGE,"E22"),sQuery(id+"F0.wireOp",EDGE,"E23"),sQuery(id+"F0.wireOp",EDGE,"E24"),sQuery(id+"F0.wireOp",EDGE,"E25"),sQuery(id+"F0.wireOp",EDGE,"E26"),sQuery(id+"F0.wireOp",EDGE,"E27"),sQuery(id+"F0.wireOp",EDGE,"E28"),sQuery(id+"F0.wireOp",EDGE,"E29"),sQuery(id+"F0.wireOp",EDGE,"E30"),sQuery(id+"F0.wireOp",EDGE,"E31"),sQuery(id+"F0.wireOp",EDGE,"E32"),sQuery(id+"F0.wireOp",EDGE,"E33"),sQuery(id+"F0.wireOp",EDGE,"E34"),sQuery(id+"F0.wireOp",EDGE,"E35"),sQuery(id+"F0.wireOp",EDGE,"E36"),sQuery(id+"F0.wireOp",EDGE,"E37"),sQuery(id+"F0.wireOp",EDGE,"E38"),sQuery(id+"F0.wireOp",EDGE,"E39"),sQuery(id+"F0.wireOp",EDGE,"E40"),sQuery(id+"F0.wireOp",EDGE,"E41"),sQuery(id+"F0.wireOp",EDGE,"E42"),sQuery(id+"F0.wireOp",EDGE,"E43"),sQuery(id+"F0.wireOp",EDGE,"E44"),sQuery(id+"F0.wireOp",EDGE,"E45"),sQuery(id+"F0.wireOp",EDGE,"E46"),sQuery(id+"F0.wireOp",EDGE,"E47"),sQuery(id+"F0.wireOp",EDGE,"E48"),sQuery(id+"F0.wireOp",EDGE,"E49"),sQuery(id+"F0.wireOp",EDGE,"E50"),sQuery(id+"F0.wireOp",EDGE,"E51"),sQuery(id+"F0.wireOp",EDGE,"E52"),sQuery(id+"F0.wireOp",EDGE,"E53"),sQuery(id+"F0.wireOp",EDGE,"E54"),sQuery(id+"F0.wireOp",EDGE,"E55"),sQuery(id+"F0.wireOp",EDGE,"E56"),sQuery(id+"F0.wireOp",EDGE,"E57"),sQuery(id+"F0.wireOp",EDGE,"E58"),sQuery(id+"F0.wireOp",EDGE,"E59"),sQuery(id+"F0.wireOp",EDGE,"E60"),sQuery(id+"F0.wireOp",EDGE,"E61"),sQuery(id+"F0.wireOp",EDGE,"E62"),sQuery(id+"F0.wireOp",EDGE,"E63"),sQuery(id+"F0.wireOp",EDGE,"E64"),sQuery(id+"F0.wireOp",EDGE,"E65"),sQuery(id+"F0.wireOp",EDGE,"E66"),sQuery(id+"F0.wireOp",EDGE,"E67"),sQuery(id+"F0.wireOp",EDGE,"E68"),sQuery(id+"F0.wireOp",EDGE,"E69"),sQuery(id+"F0.wireOp",EDGE,"E70"),sQuery(id+"F0.wireOp",EDGE,"E71"),sQuery(id+"F0.wireOp",EDGE,"E72"),sQuery(id+"F0.wireOp",EDGE,"E73"),sQuery(id+"F0.wireOp",EDGE,"E74"),sQuery(id+"F0.wireOp",EDGE,"E75"),sQuery(id+"F0.wireOp",EDGE,"E76"),sQuery(id+"F0.wireOp",EDGE,"E77"),sQuery(id+"F0.wireOp",EDGE,"E78"),sQuery(id+"F0.wireOp",EDGE,"E79"),sQuery(id+"F0.wireOp",EDGE,"E80"),sQuery(id+"F0.wireOp",EDGE,"E81"),sQuery(id+"F0.wireOp",EDGE,"E82"),sQuery(id+"F0.wireOp",EDGE,"E83"),sQuery(id+"F0.wireOp",EDGE,"E84"),sQuery(id+"F0.wireOp",EDGE,"E85"),sQuery(id+"F0.wireOp",EDGE,"E86"),sQuery(id+"F0.wireOp",EDGE,"E87"),sQuery(id+"F0.wireOp",EDGE,"E88"),sQuery(id+"F0.wireOp",EDGE,"E89"),sQuery(id+"F0.wireOp",EDGE,"E90"),sQuery(id+"F0.wireOp",EDGE,"E91"),sQuery(id+"F0.wireOp",EDGE,"E92"),sQuery(id+"F0.wireOp",EDGE,"E93"),sQuery(id+"F0.wireOp",EDGE,"E94"),sQuery(id+"F0.wireOp",EDGE,"E95"),sQuery(id+"F0.wireOp",EDGE,"E96"),sQuery(id+"F0.wireOp",EDGE,"E97"),sQuery(id+"F0.wireOp",EDGE,"E98"),sQuery(id+"F0.wireOp",EDGE,"E99"),sQuery(id+"F0.wireOp",EDGE,"E100"),sQuery(id+"F0.wireOp",EDGE,"E101"),sQuery(id+"F0.wireOp",EDGE,"E102"),sQuery(id+"F0.wireOp",EDGE,"E103"),sQuery(id+"F0.wireOp",EDGE,"E104"),sQuery(id+"F0.wireOp",EDGE,"E105"),sQuery(id+"F0.wireOp",EDGE,"E106"),sQuery(id+"F0.wireOp",EDGE,"E107"),sQuery(id+"F0.wireOp",EDGE,"E108"),sQuery(id+"F0.wireOp",EDGE,"E109"),sQuery(id+"F0.wireOp",EDGE,"E110"),sQuery(id+"F0.wireOp",EDGE,"E111"),sQuery(id+"F0.wireOp",EDGE,"E112"),sQuery(id+"F0.wireOp",EDGE,"E113"),sQuery(id+"F0.wireOp",EDGE,"E114"),sQuery(id+"F0.wireOp",EDGE,"E115"),sQuery(id+"F0.wireOp",EDGE,"E116"),sQuery(id+"F0.wireOp",EDGE,"E117"),sQuery(id+"F0.wireOp",EDGE,"E118"),sQuery(id+"F0.wireOp",EDGE,"E119"),sQuery(id+"F0.wireOp",EDGE,"E120"),sQuery(id+"F0.wireOp",EDGE,"E121"),sQuery(id+"F0.wireOp",EDGE,"E122"),sQuery(id+"F0.wireOp",EDGE,"E123"),sQuery(id+"F0.wireOp",EDGE,"E124"),sQuery(id+"F0.wireOp",EDGE,"E125"),sQuery(id+"F0.wireOp",EDGE,"E126"),sQuery(id+"F0.wireOp",EDGE,"E127"),sQuery(id+"F0.wireOp",EDGE,"E128"),sQuery(id+"F0.wireOp",EDGE,"E129"),sQuery(id+"F0.wireOp",EDGE,"E130"),sQuery(id+"F0.wireOp",EDGE,"E131"),sQuery(id+"F0.wireOp",EDGE,"E132"),sQuery(id+"F0.wireOp",EDGE,"E133"),sQuery(id+"F0.wireOp",EDGE,"E134"),sQuery(id+"F0.wireOp",EDGE,"E135"),sQuery(id+"F0.wireOp",EDGE,"E136"),sQuery(id+"F0.wireOp",EDGE,"E137"),sQuery(id+"F0.wireOp",EDGE,"E138"),sQuery(id+"F0.wireOp",EDGE,"E139"),sQuery(id+"F0.wireOp",EDGE,"E140"),sQuery(id+"F0.wireOp",EDGE,"E141"),sQuery(id+"F0.wireOp",EDGE,"E142"),sQuery(id+"F0.wireOp",EDGE,"E143"),sQuery(id+"F0.wireOp",EDGE,"E144"),sQuery(id+"F0.wireOp",EDGE,"E145"),sQuery(id+"F0.wireOp",EDGE,"E146"),sQuery(id+"F0.wireOp",EDGE,"E147"),sQuery(id+"F0.wireOp",EDGE,"E148"),sQuery(id+"F0.wireOp",EDGE,"E149"),sQuery(id+"F0.wireOp",EDGE,"E150"),sQuery(id+"F0.wireOp",EDGE,"E151"),sQuery(id+"F0.wireOp",EDGE,"E152"),sQuery(id+"F0.wireOp",EDGE,"E153"),sQuery(id+"F0.wireOp",EDGE,"E154"),sQuery(id+"F0.wireOp",EDGE,"E155"),sQuery(id+"F0.wireOp",EDGE,"E156"),sQuery(id+"F0.wireOp",EDGE,"E157"),sQuery(id+"F0.wireOp",EDGE,"E158"),sQuery(id+"F0.wireOp",EDGE,"E159"),sQuery(id+"F0.wireOp",EDGE,"E160"),sQuery(id+"F0.wireOp",EDGE,"E161"),sQuery(id+"F0.wireOp",EDGE,"E162"),sQuery(id+"F0.wireOp",EDGE,"E163"),sQuery(id+"F0.wireOp",EDGE,"E164"),sQuery(id+"F0.wireOp",EDGE,"E165"),sQuery(id+"F0.wireOp",EDGE,"E166"),sQuery(id+"F0.wireOp",EDGE,"E167"),sQuery(id+"F0.wireOp",EDGE,"E168"),sQuery(id+"F0.wireOp",EDGE,"E169"),sQuery(id+"F0.wireOp",EDGE,"E170"),sQuery(id+"F0.wireOp",EDGE,"E171"),sQuery(id+"F0.wireOp",EDGE,"E172"),sQuery(id+"F0.wireOp",EDGE,"E173"),sQuery(id+"F0.wireOp",EDGE,"E174"),sQuery(id+"F0.wireOp",EDGE,"E175"),sQuery(id+"F0.wireOp",EDGE,"E176"),sQuery(id+"F0.wireOp",EDGE,"E177"),sQuery(id+"F0.wireOp",EDGE,"E178"),sQuery(id+"F0.wireOp",EDGE,"E179"),sQuery(id+"F0.wireOp",EDGE,"E180"),sQuery(id+"F0.wireOp",EDGE,"E181"),sQuery(id+"F0.wireOp",EDGE,"E182"),sQuery(id+"F0.wireOp",EDGE,"E183"),sQuery(id+"F0.wireOp",EDGE,"E184"),sQuery(id+"F0.wireOp",EDGE,"E185"),sQuery(id+"F0.wireOp",EDGE,"E186"),sQuery(id+"F0.wireOp",EDGE,"E187"),sQuery(id+"F0.wireOp",EDGE,"E188"),sQuery(id+"F0.wireOp",EDGE,"E189"),sQuery(id+"F0.wireOp",EDGE,"E190"),sQuery(id+"F0.wireOp",EDGE,"E191"),sQuery(id+"F0.wireOp",EDGE,"E192"),sQuery(id+"F0.wireOp",EDGE,"E193"),sQuery(id+"F0.wireOp",EDGE,"E194"),sQuery(id+"F0.wireOp",EDGE,"E195"),sQuery(id+"F0.wireOp",EDGE,"E196"),sQuery(id+"F0.wireOp",EDGE,"E197"),sQuery(id+"F0.wireOp",EDGE,"E198"),sQuery(id+"F0.wireOp",EDGE,"E199"),sQuery(id+"F0.wireOp",EDGE,"E200"),sQuery(id+"F0.wireOp",EDGE,"E201"),sQuery(id+"F0.wireOp",EDGE,"E202"),sQuery(id+"F0.wireOp",EDGE,"E203"),sQuery(id+"F0.wireOp",EDGE,"E204"),sQuery(id+"F0.wireOp",EDGE,"E205"),sQuery(id+"F0.wireOp",EDGE,"E206"),sQuery(id+"F0.wireOp",EDGE,"E207")])],"isStart":true});
            extrude(context, id + "F3", {"entities" : qUnion([Q0]), "operationType" : NewBodyOperationType.ADD, "endBound" : BoundingType.UP_TO_SURFACE, "oppositeDirection" : true, "endBoundEntityFace" : qUnion([Q1]), "depth" : 2 * mm});
        }
    });
